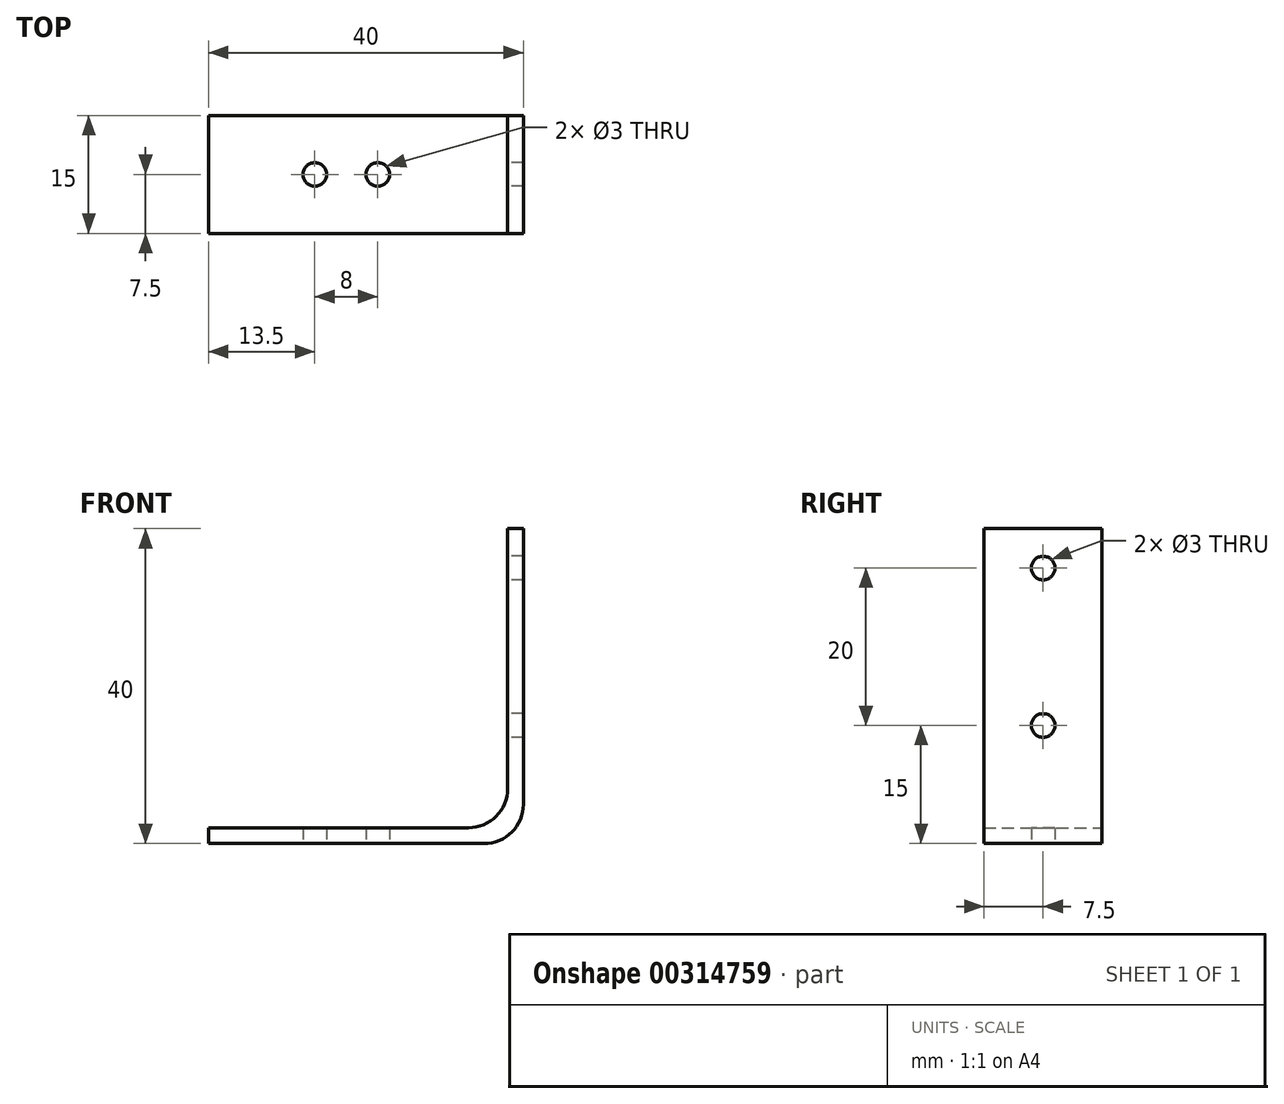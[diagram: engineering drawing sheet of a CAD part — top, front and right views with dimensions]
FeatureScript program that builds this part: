
annotation { "Feature Type Name" : "Feature", "Feature Type Description" : "" }
export const myFeature = defineFeature(function(context is Context, id is Id, definition is map)
    precondition{}
    {
        {
            var Q0;
            Q0=qCreatedBy(makeId("Front.planeOp"),FACE);
            var sketch = newSketch(context, id + "F0", { "sketchPlane" : qUnion([Q0])});
            skLineSegment(sketch, "E0.bottom", {"start": v(0, 0) * mm, "end": v(-2, 0) * mm});
            skLineSegment(sketch, "E0.right", {"start": v(-2, 0) * mm, "end": v(-2, -38) * mm});
            skLineSegment(sketch, "E1.bottom", {"start": v(-2, -38) * mm, "end": v(-40, -38) * mm});
            skLineSegment(sketch, "E1.top", {"start": v(0, -40) * mm, "end": v(-40, -40) * mm});
            skLineSegment(sketch, "E1.right", {"start": v(-40, -38) * mm, "end": v(-40, -40) * mm});
            skLineSegment(sketch, "E2", {"start": v(0, 0) * mm, "end": v(0, -40) * mm});
            skSolve(sketch);
        }
        {
            var Q0;
            Q0=makeQuery(id+"F0.imprint","IMPRINT",FACE,{"disambiguationData":[TD([[makeQuery(id+"F0.imprint","IMPRINT",EDGE,{"derivedFrom":sQuery(id+"F0.wireOp",EDGE,"E0.bottom")}),1.0]])]});
            extrude(context, id + "F1", {"entities" : qUnion([Q0]), "depth" : 15 * mm});
        }
        {
            var Q0;
            Q0=makeQuery(id+"F1.opExtrude","SWEPT_EDGE",EDGE,{"disambiguationData":[OSD([sQuery(id+"F0.wireOp",EDGE,"E1.top"),sQuery(id+"F0.wireOp",EDGE,"E2")])]});
            var Q1;
            Q1=makeQuery(id+"F1.opExtrude","SWEPT_EDGE",EDGE,{"disambiguationData":[OSD([sQuery(id+"F0.wireOp",EDGE,"E0.right"),sQuery(id+"F0.wireOp",EDGE,"E1.bottom")])]});
            fillet(context, id + "F2", {"entities" : qUnion([Q0, Q1]), "radius" : 5 * mm, "tangentPropagation" : true, "allowEdgeOverflow" : false});
        }
        {
            var Q0;
            Q0=makeQuery(id+"F1.opExtrude","SWEPT_FACE",FACE,{"disambiguationData":[OSD([sQuery(id+"F0.wireOp",EDGE,"E0.right")])]});
            var sketch = newSketch(context, id + "F3", { "sketchPlane" : qUnion([Q0])});
            skCircle(sketch, "E3", {"center": v(7.5, -25) * mm, "radius": 1.5 * mm});
            skCircle(sketch, "E4", {"center": v(7.5, -5) * mm, "radius": 1.5 * mm});
            skPoint(sketch, "E5.orphan", {"position": v(7.5, 0) * mm});
            skPoint(sketch, "E6.orphan", {"position": v(0, -16.5) * mm});
            skPoint(sketch, "E7.start.orphan", {"position": v(15, -16.5) * mm});
            skPoint(sketch, "E8.end.orphan", {"position": v(7.5, -33) * mm});
            skPoint(sketch, "E9.orphan", {"position": v(0, -5) * mm});
            skPoint(sketch, "E10.orphan", {"position": v(0, -25) * mm});
            skSolve(sketch);
        }
        {
            var Q0;
            Q0=sQuery(id+"F3.wireOp",VERTEX,"E4.center");
            var Q1;
            Q1=sQuery(id+"F3.wireOp",VERTEX,"E3.center");
            var Q2;
            Q2=makeQuery(id+"F1.opExtrude","SWEPT_BODY",BODY,{"disambiguationData":[OSD([sQuery(id+"F0.wireOp",EDGE,"E0.bottom"),sQuery(id+"F0.wireOp",EDGE,"E0.left"),sQuery(id+"F0.wireOp",EDGE,"E0.right"),sQuery(id+"F0.wireOp",EDGE,"E1.bottom"),sQuery(id+"F0.wireOp",EDGE,"E1.top"),sQuery(id+"F0.wireOp",EDGE,"E1.left"),sQuery(id+"F0.wireOp",EDGE,"E1.right")])]});
            hole(context, id + "F4", {"style" : HoleStyle.SIMPLE, "endStyle" : HoleEndStyle.THROUGH, "holeDiameter" : 3 * mm, "isTappedThrough" : true, "tappedDepth" : 12 * mm, "tapClearance" : 3, "locations" : qUnion([Q0, Q1]), "scope" : qUnion([Q2])});
        }
        {
            var Q0;
            Q0=makeQuery(id+"F1.opExtrude","SWEPT_FACE",FACE,{"disambiguationData":[OSD([sQuery(id+"F0.wireOp",EDGE,"E1.top")])]});
            var sketch = newSketch(context, id + "F5", { "sketchPlane" : qUnion([Q0])});
            skCircle(sketch, "E11", {"center": v(-26.5, 7.5) * mm, "radius": 1 * mm});
            skPoint(sketch, "E12.orphan", {"position": v(-40, 7.5) * mm});
            skCircle(sketch, "E13", {"center": v(-18.5, 7.5) * mm, "radius": 1 * mm});
            skLineSegment(sketch, "E14", {"start": v(-26.5, 7.5) * mm, "end": v(-26.5, 15) * mm});
            skLineSegment(sketch, "E15", {"start": v(-18.5, 7.5) * mm, "end": v(-18.5, 15) * mm});
            skSolve(sketch);
        }
        {
            var Q0;
            Q0=sQuery(id+"F5.wireOp",VERTEX,"E11.center");
            var Q1;
            Q1=sQuery(id+"F5.wireOp",VERTEX,"E13.center");
            var Q2;
            Q2=makeQuery(id+"F1.opExtrude","SWEPT_BODY",BODY,{"disambiguationData":[OSD([sQuery(id+"F0.wireOp",EDGE,"E0.bottom"),sQuery(id+"F0.wireOp",EDGE,"E0.left"),sQuery(id+"F0.wireOp",EDGE,"E0.right"),sQuery(id+"F0.wireOp",EDGE,"E1.bottom"),sQuery(id+"F0.wireOp",EDGE,"E1.top"),sQuery(id+"F0.wireOp",EDGE,"E1.left"),sQuery(id+"F0.wireOp",EDGE,"E1.right")])]});
            hole(context, id + "F6", {"style" : HoleStyle.SIMPLE, "endStyle" : HoleEndStyle.THROUGH, "holeDiameter" : 3 * mm, "isTappedThrough" : true, "tappedDepth" : 12 * mm, "tapClearance" : 3, "locations" : qUnion([Q0, Q1]), "scope" : qUnion([Q2])});
        }
    });
